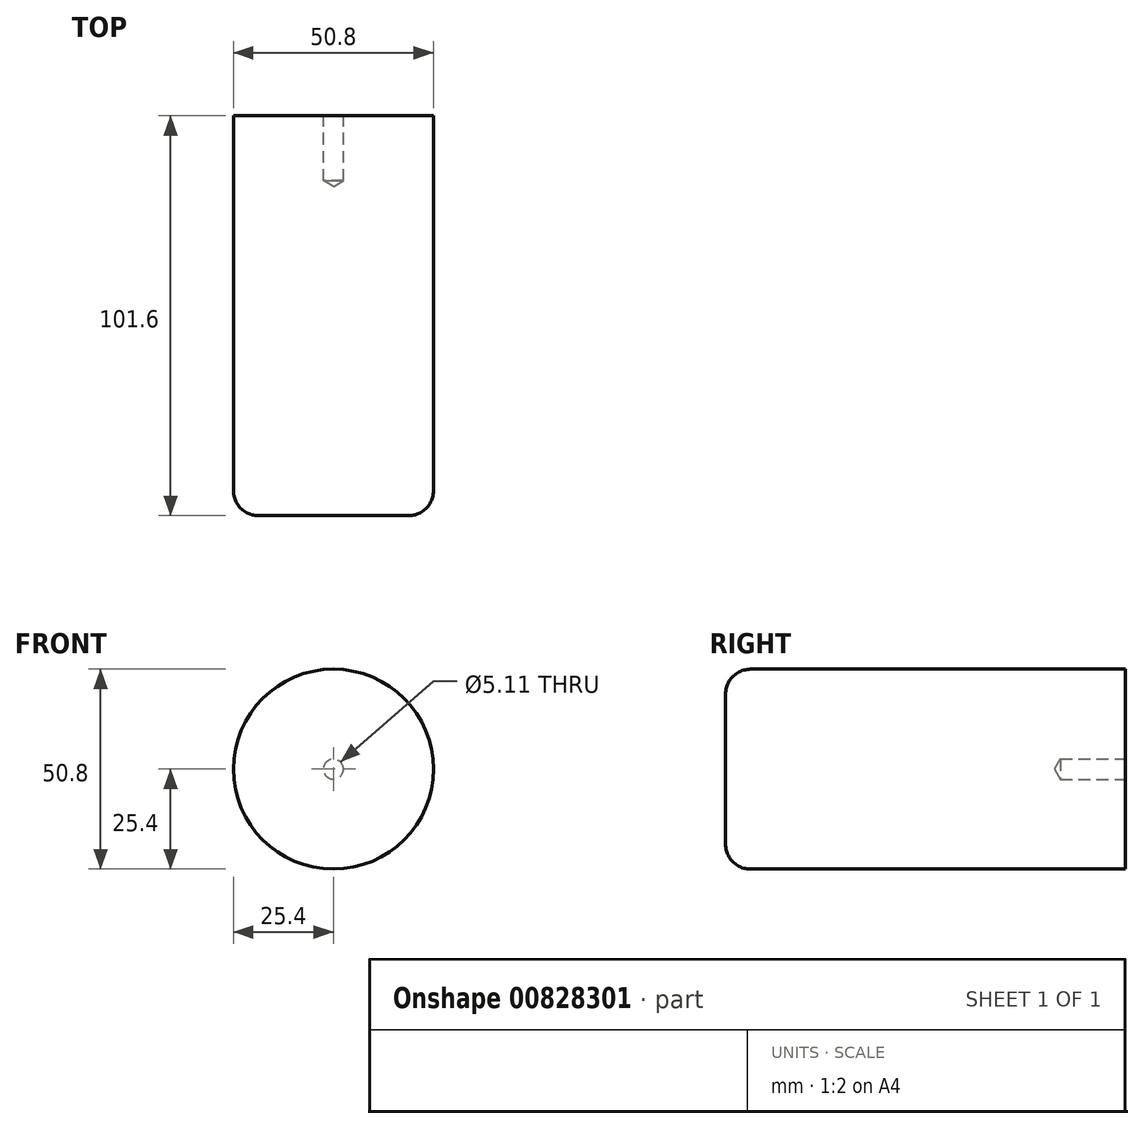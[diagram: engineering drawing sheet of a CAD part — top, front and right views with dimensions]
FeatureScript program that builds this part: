
annotation { "Feature Type Name" : "Feature", "Feature Type Description" : "" }
export const myFeature = defineFeature(function(context is Context, id is Id, definition is map)
    precondition{}
    {
        {
            var Q0;
            Q0=qCreatedBy(makeId("Front.planeOp"),FACE);
            var sketch = newSketch(context, id + "F0", { "sketchPlane" : qUnion([Q0])});
            skCircle(sketch, "E0", {"center": v(0, 0) * mm, "radius": 25.4 * mm});
            skSolve(sketch);
        }
        {
            var Q0;
            Q0=makeQuery(id+"F0.imprint","IMPRINT",FACE,{"disambiguationData":[TD([[makeQuery(id+"F0.imprint","IMPRINT",EDGE,{"derivedFrom":sQuery(id+"F0.wireOp",EDGE,"E0")}),1.0]])]});
            extrude(context, id + "F1", {"entities" : qUnion([Q0]), "depth" : 101.6 * mm, "offsetDistance" : 25.4 * mm});
        }
        {
            var Q0;
            Q0=makeQuery(id+"F1.opExtrude","CAP_EDGE",EDGE,{"disambiguationData":[OSD([sQuery(id+"F0.wireOp",EDGE,"E0")])],"isStart":false});
            fillet(context, id + "F2", {"entities" : qUnion([Q0]), "radius" : 6.35 * mm, "tangentPropagation" : true, "allowEdgeOverflow" : false});
        }
        {
            var Q0;
            Q0=makeQuery(id+"F1.opExtrude","CAP_FACE",FACE,{"disambiguationData":[OSD([sQuery(id+"F0.wireOp",EDGE,"E0")])],"isStart":true});
            var sketch = newSketch(context, id + "F3", { "sketchPlane" : qUnion([Q0])});
            skCircle(sketch, "E1", {"center": v(0, 0) * mm, "radius": 6.85 * mm});
            skSolve(sketch);
        }
        {
            var Q0;
            Q0=sQuery(id+"F3.wireOp",VERTEX,"E1.center");
            var Q1;
            Q1=makeQuery(id+"F1.opExtrude","SWEPT_BODY",BODY,{"disambiguationData":[OSD([sQuery(id+"F0.wireOp",EDGE,"E0")])]});
            hole(context, id + "F4", {"style" : HoleStyle.SIMPLE, "endStyle" : HoleEndStyle.BLIND, "standardTappedOrClearance" : lookupTablePath({ "standard" : "ANSI", "engagement" : "75%", "pitch" : "20 tpi", "size" : "1/4", "type" : "Tapped" }), "standardBlindInLast" : lookupTablePath({ "standard" : "ANSI", "engagement" : "75%", "pitch" : "20 tpi", "size" : "1/4", "type" : "Tapped" }), "holeDiameter" : 5.1 * mm, "majorDiameter" : 6.35 * mm, "showTappedDepth" : true, "holeDepth" : 16.51 * mm, "isTappedThrough" : true, "tappedDepth" : 12.7 * mm, "tapClearance" : 3, "locations" : qUnion([Q0]), "scope" : qUnion([Q1])});
        }
    });
